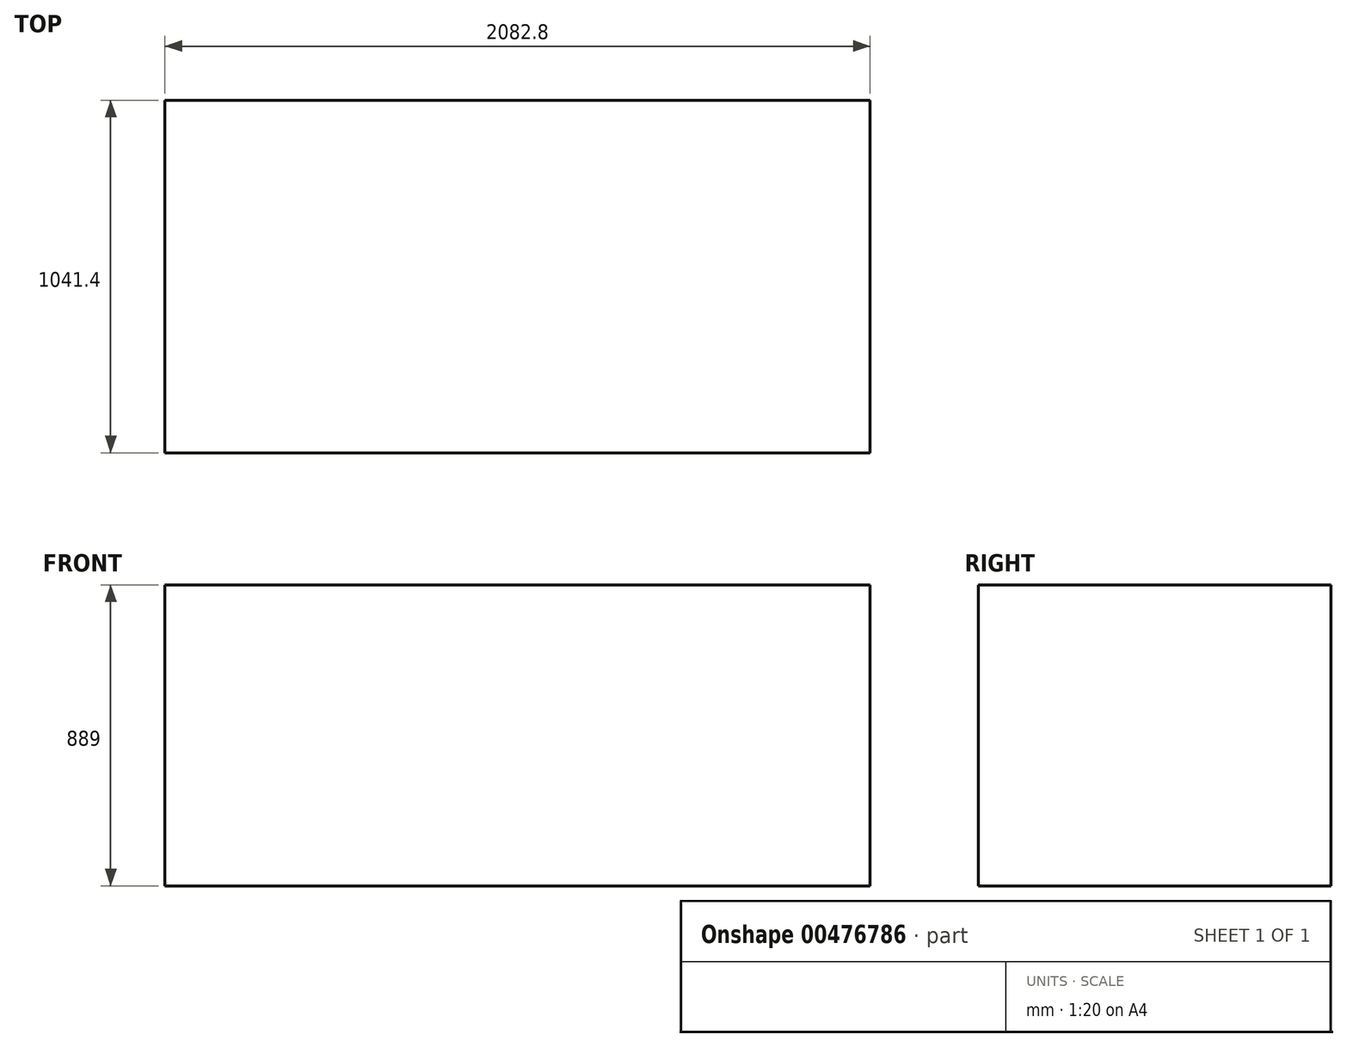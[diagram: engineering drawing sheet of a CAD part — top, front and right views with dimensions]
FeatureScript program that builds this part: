
annotation { "Feature Type Name" : "Feature", "Feature Type Description" : "" }
export const myFeature = defineFeature(function(context is Context, id is Id, definition is map)
    precondition{}
    {
        {
            var Q0;
            Q0=qCreatedBy(makeId("Top.planeOp"),FACE);
            var sketch = newSketch(context, id + "F0", { "sketchPlane" : qUnion([Q0])});
            skLineSegment(sketch, "E0.bottom", {"start": v(0, 0) * mm, "end": v(2082.8, 0) * mm});
            skLineSegment(sketch, "E0.top", {"start": v(0, 1041.4) * mm, "end": v(2082.8, 1041.4) * mm});
            skLineSegment(sketch, "E0.left", {"start": v(0, 0) * mm, "end": v(0, 1041.4) * mm});
            skLineSegment(sketch, "E0.right", {"start": v(2082.8, 0) * mm, "end": v(2082.8, 1041.4) * mm});
            skSolve(sketch);
        }
        {
            var Q0;
            Q0=qSketchRegion(id+"F0",true);
            extrude(context, id + "F1", {"entities" : qUnion([Q0]), "depth" : 889 * mm});
        }
    });
